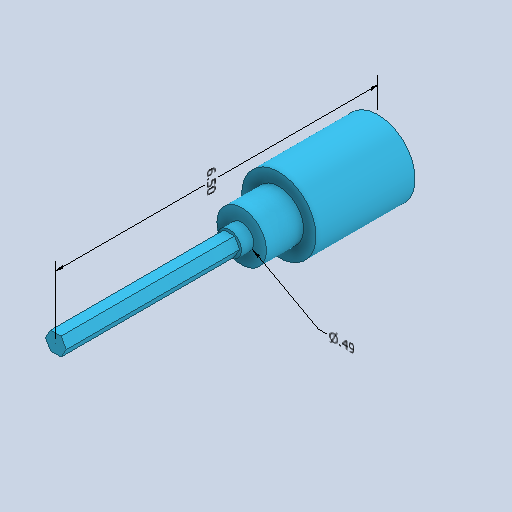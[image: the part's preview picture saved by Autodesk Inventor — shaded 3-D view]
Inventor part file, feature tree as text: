
AUTODESK INVENTOR PART (.ipt)
format: ipt  version: 2022.1 (Build 261234000, 234)  size: 156,672 bytes
history: native  units: in
note: dims shown in document units (in); Inventor stores cm internally (conversion verified against a paired STEP export)
features: other x5, extrude x4, sketch x4
ambient origin geometry x8: Origin, YZ Plane, XZ Plane, XY Plane, X Axis, Y Axis, Z Axis, Center Point
bodies: Body1 (feature_tree)
feature tree (13):
  other  "Annotations"
  extrude  "Extrusion2"  Depth=4.5in TaperAngle=0.0deg
  extrude  "Extrusion4"  Depth=1.0in
  other  "Reduce Hex Shaft"
  extrude  "Extrusion5"  Depth=0.75in
  other  "Reduce Base Bushing"
  extrude  "Extrusion7"  Depth=0.5in
  sketch  "Sketch1"  dims[d0=0.375in d4=4.5in d5=0.0in]
  sketch  "Sketch4"  dims[d6=0.001in d10=1.0in]
  sketch  "Sketch5"  dims[d11=0.75in d12=0.0in d13=0.005in]
  sketch  "Sketch8"  dims[d14=0.005in d15=0.5in d16=0.25in d17=0.0in d20=0.005in d21=0.005in d28=1.5in d29=2.0in d30=0.0in d23=2.2764in d24=0.49in d31=6.5in]
  other  "Diameter Dimension 1"
  other  "Linear Dimension 1"
